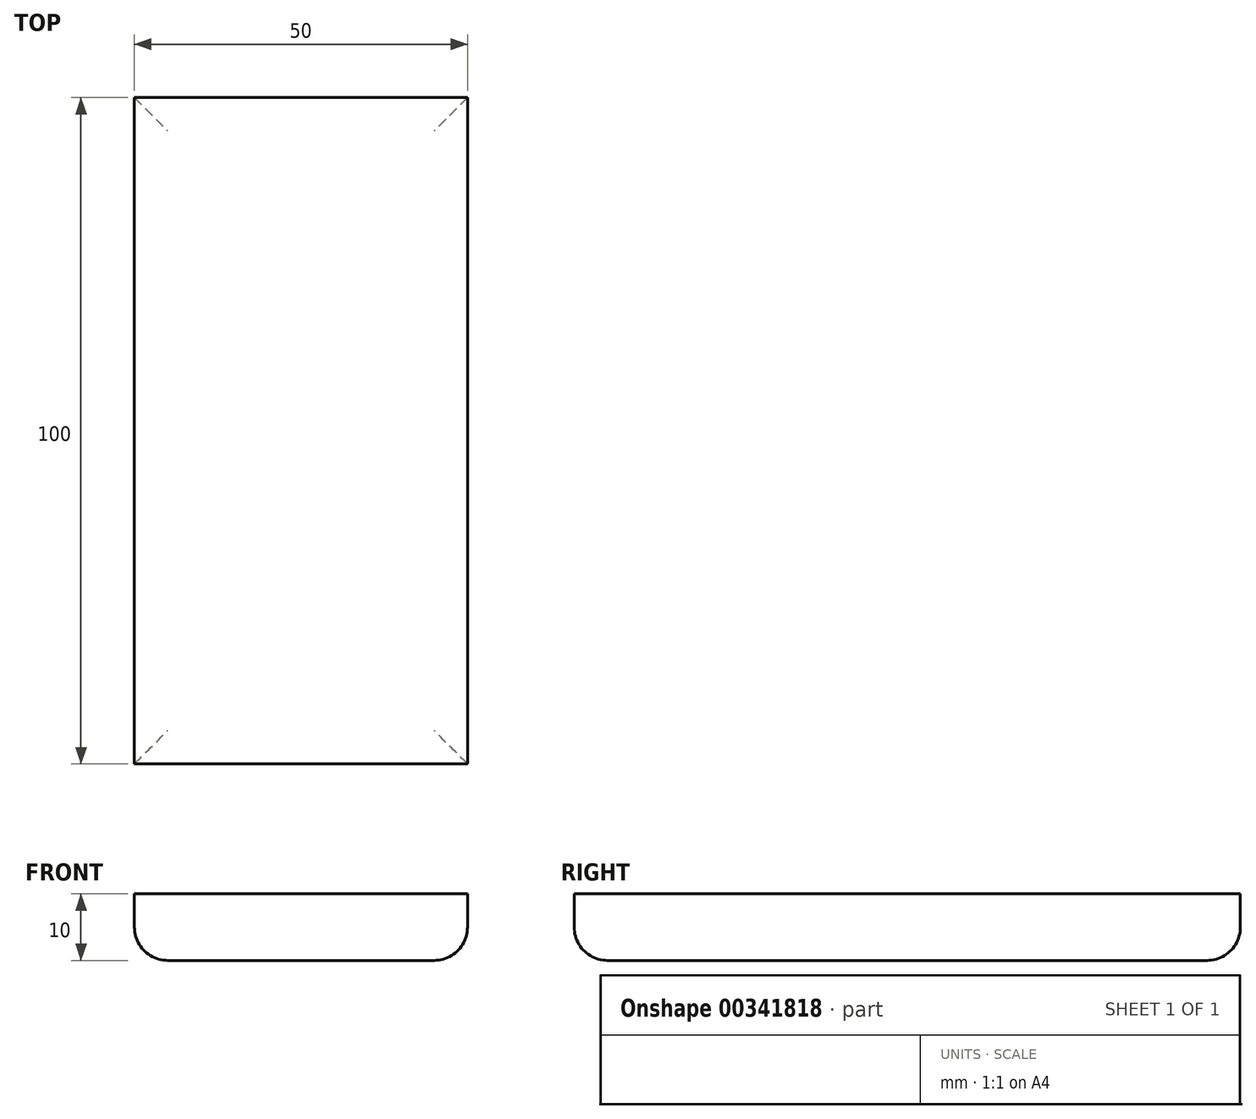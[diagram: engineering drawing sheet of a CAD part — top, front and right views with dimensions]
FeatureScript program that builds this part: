
annotation { "Feature Type Name" : "Feature", "Feature Type Description" : "" }
export const myFeature = defineFeature(function(context is Context, id is Id, definition is map)
    precondition{}
    {
        {
            var Q0;
            Q0=qCreatedBy(makeId("Top.planeOp"),FACE);
            var sketch = newSketch(context, id + "F0", { "sketchPlane" : qUnion([Q0])});
            skLineSegment(sketch, "E0.bottom", {"start": v(0, 0) * mm, "end": v(50, 0) * mm});
            skLineSegment(sketch, "E0.top", {"start": v(0, 100) * mm, "end": v(50, 100) * mm});
            skLineSegment(sketch, "E0.left", {"start": v(0, 0) * mm, "end": v(0, 100) * mm});
            skLineSegment(sketch, "E0.right", {"start": v(50, 0) * mm, "end": v(50, 100) * mm});
            skSolve(sketch);
        }
        {
            var Q0;
            Q0=makeQuery(id+"F0.imprint","IMPRINT",FACE,{"disambiguationData":[TD([[makeQuery(id+"F0.imprint","IMPRINT",EDGE,{"derivedFrom":sQuery(id+"F0.wireOp",EDGE,"E0.bottom")}),1.0]])]});
            extrude(context, id + "F1", {"entities" : qUnion([Q0]), "depth" : 10 * mm});
        }
        {
            var Q0;
            Q0=makeQuery(id+"F1.opExtrude","CAP_EDGE",EDGE,{"disambiguationData":[OSD([sQuery(id+"F0.wireOp",EDGE,"E0.right")])],"isStart":true});
            var Q1;
            Q1=makeQuery(id+"F1.opExtrude","CAP_FACE",FACE,{"disambiguationData":[OSD([sQuery(id+"F0.wireOp",EDGE,"E0.bottom"),sQuery(id+"F0.wireOp",EDGE,"E0.top"),sQuery(id+"F0.wireOp",EDGE,"E0.left"),sQuery(id+"F0.wireOp",EDGE,"E0.right")])],"isStart":true});
            fillet(context, id + "F2", {"entities" : qUnion([Q0, Q1]), "radius" : 5 * mm, "tangentPropagation" : true, "allowEdgeOverflow" : false});
        }
    });
